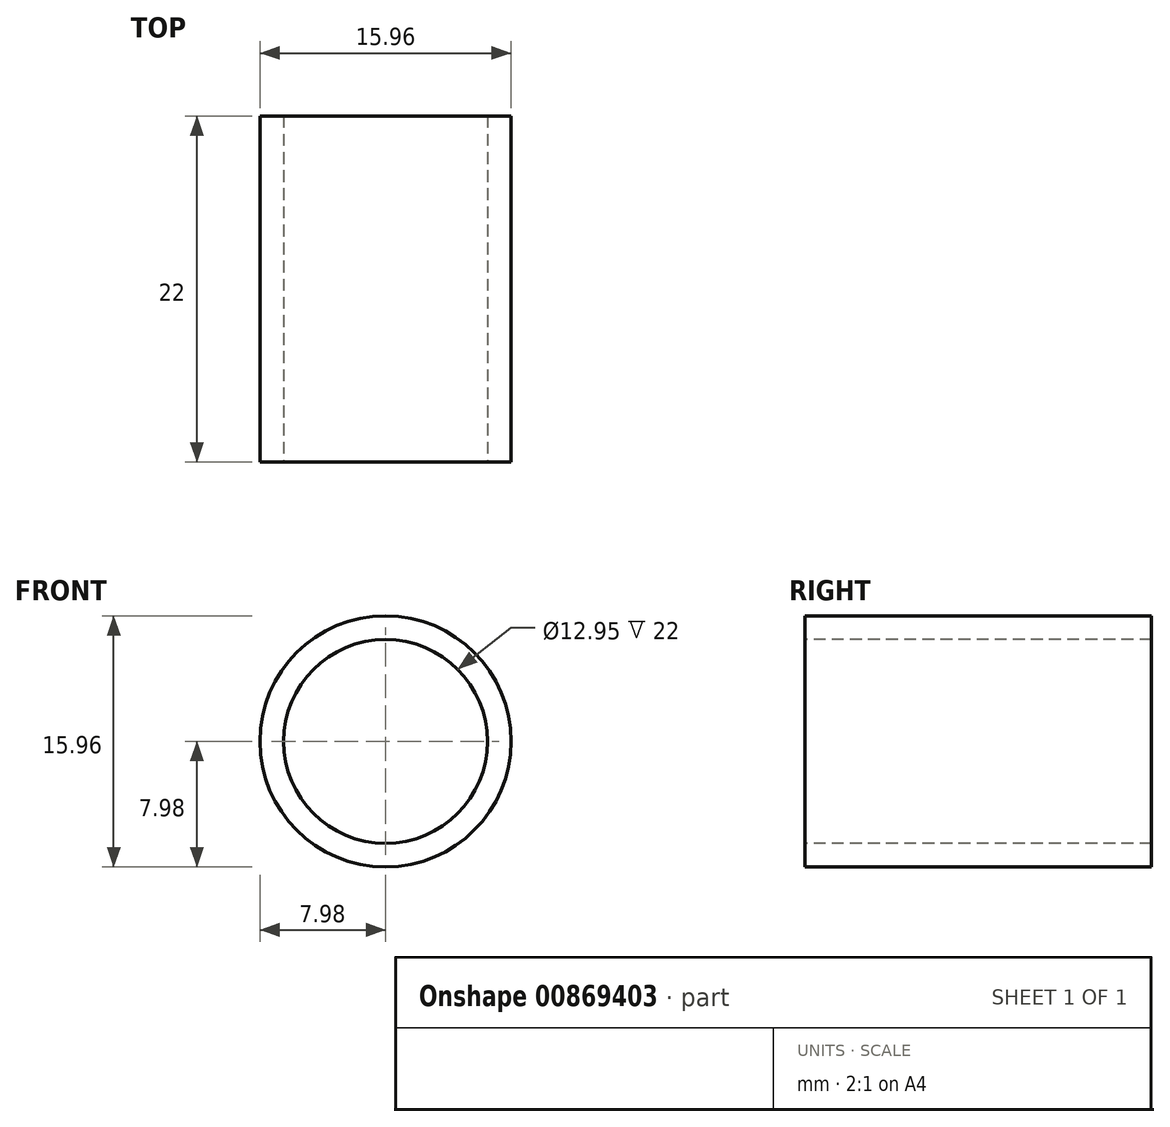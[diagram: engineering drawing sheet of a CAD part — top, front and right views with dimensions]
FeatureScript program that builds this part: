
annotation { "Feature Type Name" : "Feature", "Feature Type Description" : "" }
export const myFeature = defineFeature(function(context is Context, id is Id, definition is map)
    precondition{}
    {
        {
            var Q0;
            Q0=qCreatedBy(makeId("Front.planeOp"),FACE);
            var sketch = newSketch(context, id + "F0", { "sketchPlane" : qUnion([Q0])});
            skCircle(sketch, "E0", {"center": v(0, 0) * mm, "radius": 7.97 * mm});
            skCircle(sketch, "E1", {"center": v(0, 0) * mm, "radius": 6.47 * mm});
            skSolve(sketch);
        }
        {
            var Q0;
            Q0=makeQuery(id+"F0.imprint","IMPRINT",FACE,{"disambiguationData":[TD([[makeQuery(id+"F0.imprint","IMPRINT",EDGE,{"derivedFrom":sQuery(id+"F0.wireOp",EDGE,"E0")}),1.0]])]});
            extrude(context, id + "F1", {"entities" : qUnion([Q0]), "oppositeDirection" : true, "depth" : 22 * mm, "offsetDistance" : 25 * mm});
        }
    });
